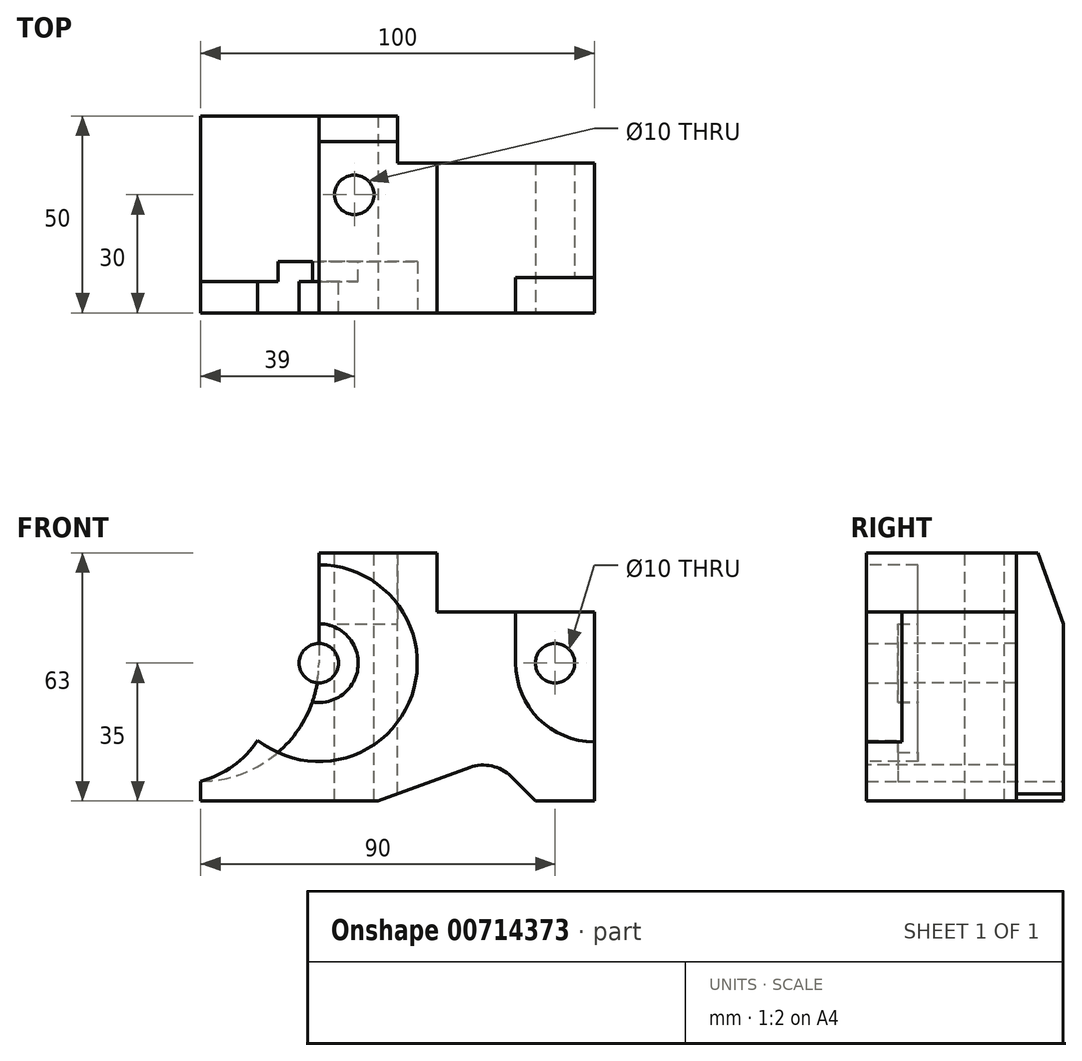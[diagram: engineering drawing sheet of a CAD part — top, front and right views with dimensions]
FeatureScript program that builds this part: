
annotation { "Feature Type Name" : "Feature", "Feature Type Description" : "" }
export const myFeature = defineFeature(function(context is Context, id is Id, definition is map)
    precondition{}
    {
        {
            var Q0;
            Q0=qCreatedBy(makeId("Front.planeOp"),FACE);
            var sketch = newSketch(context, id + "F0", { "sketchPlane" : qUnion([Q0])});
            skLineSegment(sketch, "E0", {"start": v(0, 0) * mm, "end": v(0, 63) * mm});
            skLineSegment(sketch, "E1", {"start": v(0, 63) * mm, "end": v(100, 63) * mm});
            skLineSegment(sketch, "E2", {"start": v(100, 63) * mm, "end": v(100, 0) * mm});
            skLineSegment(sketch, "E3", {"start": v(100, 0) * mm, "end": v(0, 0) * mm});
            skSolve(sketch);
        }
        {
            var Q0;
            Q0 = qSketchRegion(id + "F0", true);
            extrude(context, id + "F1", {"entities" : qUnion([Q0]), "oppositeDirection" : true, "depth" : 50 * mm, "offsetDistance" : 25 * mm});
        }
        {
            var Q0;
            Q0=makeQuery(id+"F1.opExtrude","CAP_FACE",FACE,{"disambiguationData":[OSD([sQuery(id+"F0.wireOp",EDGE,"E0"),sQuery(id+"F0.wireOp",EDGE,"E1"),sQuery(id+"F0.wireOp",EDGE,"E2"),sQuery(id+"F0.wireOp",EDGE,"E3")])],"isStart":true});
            var sketch = newSketch(context, id + "F2", { "sketchPlane" : qUnion([Q0])});
            skLineSegment(sketch, "E4", {"start": v(60, 63) * mm, "end": v(60, 48) * mm});
            skLineSegment(sketch, "E5", {"start": v(60, 48) * mm, "end": v(100, 48) * mm});
            skLineSegment(sketch, "E6", {"start": v(100, 48) * mm, "end": v(100, 63) * mm});
            skLineSegment(sketch, "E7", {"start": v(100, 63) * mm, "end": v(60, 63) * mm});
            skLineSegment(sketch, "E8", {"start": v(80, 48) * mm, "end": v(80, 35) * mm});
            skArc(sketch, "E9", {"start": v(80, 35) * mm, "mid": v(85.86, 20.86) * mm, "end": v(100, 15) * mm});
            skSolve(sketch);
        }
        {
            var Q0;
            Q0 = qSketchRegion(id + "F2", true);
            extrude(context, id + "F3", {"entities" : qUnion([Q0]), "operationType" : NewBodyOperationType.REMOVE, "oppositeDirection" : true, "depth" : 50 * mm, "offsetDistance" : 25 * mm});
        }
        {
            var Q0;
            {var subQ3=sQuery(id+"F2.wireOp",EDGE,"E8");Q0=makeQuery(id+"F2.imprint","IMPRINT",FACE,{"disambiguationData":[TD([[makeQuery(id+"F2.imprint","IMPRINT",EDGE,{"derivedFrom":subQ3}),1.0]])]});}
            extrude(context, id + "F4", {"entities" : qUnion([Q0]), "operationType" : NewBodyOperationType.REMOVE, "oppositeDirection" : true, "depth" : 9 * mm, "offsetDistance" : 25 * mm});
        }
        {
            var Q0;
            Q0=makeQuery(id+"F4.boolean.opBoolean","COPY",FACE,{"derivedFrom":makeQuery(id+"F4.opExtrude","CAP_FACE",FACE,{"disambiguationData":[OSD([sQuery(id+"F0.wireOp",EDGE,"E2"),sQuery(id+"F2.wireOp",EDGE,"E5"),sQuery(id+"F2.wireOp",EDGE,"E8"),sQuery(id+"F2.wireOp",EDGE,"E9")])],"isStart":false})});
            var sketch = newSketch(context, id + "F5", { "sketchPlane" : qUnion([Q0])});
            skCircle(sketch, "E10", {"center": v(90, 35) * mm, "radius": 5 * mm});
            skSolve(sketch);
        }
        {
            var Q0;
            Q0 = qSketchRegion(id + "F5", true);
            extrude(context, id + "F6", {"entities" : qUnion([Q0]), "operationType" : NewBodyOperationType.REMOVE, "oppositeDirection" : true, "depth" : 50 * mm, "offsetDistance" : 25 * mm});
        }
        {
            var Q0;
            Q0=makeQuery(id+"F1.opExtrude","CAP_FACE",FACE,{"disambiguationData":[OSD([sQuery(id+"F0.wireOp",EDGE,"E0"),sQuery(id+"F0.wireOp",EDGE,"E1"),sQuery(id+"F0.wireOp",EDGE,"E2"),sQuery(id+"F0.wireOp",EDGE,"E3")])],"isStart":true});
            var sketch = newSketch(context, id + "F7", { "sketchPlane" : qUnion([Q0])});
            skLineSegment(sketch, "E11", {"start": v(45, 0) * mm, "end": v(85, 0) * mm});
            skLineSegment(sketch, "E12", {"start": v(45, 0) * mm, "end": v(68.34, 8.5) * mm});
            skLineSegment(sketch, "E13", {"start": v(85, 0) * mm, "end": v(78.83, 6.17) * mm});
            skArc(sketch, "E14", {"start": v(78.83, 6.17) * mm, "mid": v(73.92, 8.86) * mm, "end": v(68.34, 8.5) * mm});
            skSolve(sketch);
        }
        {
            var Q0;
            Q0 = qSketchRegion(id + "F7", true);
            extrude(context, id + "F8", {"entities" : qUnion([Q0]), "operationType" : NewBodyOperationType.REMOVE, "oppositeDirection" : true, "depth" : 50 * mm, "offsetDistance" : 25 * mm});
        }
        {
            var Q0;
            Q0=makeQuery(id+"F1.opExtrude","CAP_FACE",FACE,{"disambiguationData":[OSD([sQuery(id+"F0.wireOp",EDGE,"E0"),sQuery(id+"F0.wireOp",EDGE,"E1"),sQuery(id+"F0.wireOp",EDGE,"E2"),sQuery(id+"F0.wireOp",EDGE,"E3")])],"isStart":true});
            var sketch = newSketch(context, id + "F9", { "sketchPlane" : qUnion([Q0])});
            skCircle(sketch, "E15", {"center": v(30, 35) * mm, "radius": 25 * mm});
            skSolve(sketch);
        }
        {
            var Q0;
            Q0 = qSketchRegion(id + "F9", true);
            extrude(context, id + "F10", {"entities" : qUnion([Q0]), "operationType" : NewBodyOperationType.REMOVE, "oppositeDirection" : true, "depth" : 13 * mm, "offsetDistance" : 25 * mm});
        }
        {
            var Q0;
            Q0=makeQuery(id+"F10.boolean.opBoolean","COPY",FACE,{"derivedFrom":makeQuery(id+"F10.opExtrude","CAP_FACE",FACE,{"disambiguationData":[OSD([sQuery(id+"F9.wireOp",EDGE,"E15")])],"isStart":false})});
            var sketch = newSketch(context, id + "F11", { "sketchPlane" : qUnion([Q0])});
            skCircle(sketch, "E16", {"center": v(30, 35) * mm, "radius": 10 * mm});
            skSolve(sketch);
        }
        {
            var Q0;
            Q0 = qSketchRegion(id + "F11", true);
            extrude(context, id + "F12", {"entities" : qUnion([Q0]), "operationType" : NewBodyOperationType.ADD, "depth" : 5 * mm, "offsetDistance" : 25 * mm});
        }
        {
            var Q0;
            Q0=makeQuery(id+"F1.opExtrude","CAP_FACE",FACE,{"disambiguationData":[OSD([sQuery(id+"F0.wireOp",EDGE,"E0"),sQuery(id+"F0.wireOp",EDGE,"E1"),sQuery(id+"F0.wireOp",EDGE,"E2"),sQuery(id+"F0.wireOp",EDGE,"E3")])],"isStart":false});
            var sketch = newSketch(context, id + "F13", { "sketchPlane" : qUnion([Q0])});
            skLineSegment(sketch, "E17", {"start": v(-30, 63) * mm, "end": v(-30, 35) * mm});
            skArc(sketch, "E18", {"start": v(-30, 35) * mm, "mid": v(-21.21, 13.79) * mm, "end": v(0, 5) * mm});
            skLineSegment(sketch, "E19", {"start": v(-30, 63) * mm, "end": v(0, 63) * mm});
            skLineSegment(sketch, "E20", {"start": v(0, 63) * mm, "end": v(0, 5) * mm});
            skSolve(sketch);
        }
        {
            var Q0;
            Q0 = qSketchRegion(id + "F13", true);
            extrude(context, id + "F14", {"entities" : qUnion([Q0]), "operationType" : NewBodyOperationType.REMOVE, "oppositeDirection" : true, "depth" : 42 * mm, "offsetDistance" : 25 * mm});
        }
        {
            var Q0;
            Q0=makeQuery(id+"F14.boolean.opBoolean","COPY",FACE,{"derivedFrom":makeQuery(id+"F14.opExtrude","CAP_FACE",FACE,{"disambiguationData":[OSD([sQuery(id+"F13.wireOp",EDGE,"E17"),sQuery(id+"F13.wireOp",EDGE,"E18"),sQuery(id+"F13.wireOp",EDGE,"E19"),sQuery(id+"F13.wireOp",EDGE,"E20")])],"isStart":false})});
            var sketch = newSketch(context, id + "F15", { "sketchPlane" : qUnion([Q0])});
            skLineSegment(sketch, "E21", {"start": v(-30, 60) * mm, "end": v(-30, 63) * mm});
            skLineSegment(sketch, "E22", {"start": v(-30, 63) * mm, "end": v(0, 63) * mm});
            skLineSegment(sketch, "E23", {"start": v(0, 63) * mm, "end": v(0, 5) * mm});
            skArc(sketch, "E24", {"start": v(-14.47, 15.4) * mm, "mid": v(-8.2, 8.87) * mm, "end": v(0, 5) * mm});
            skArc(sketch, "E25", {"start": v(-14.47, 15.4) * mm, "mid": v(-6.4, 43.22) * mm, "end": v(-30, 60) * mm});
            skSolve(sketch);
        }
        {
            var Q0;
            Q0 = qSketchRegion(id + "F15", true);
            extrude(context, id + "F16", {"entities" : qUnion([Q0]), "operationType" : NewBodyOperationType.REMOVE, "oppositeDirection" : true, "depth" : 8 * mm, "offsetDistance" : 25 * mm});
        }
        {
            var Q0;
            Q0=makeQuery(id+"F12.opExtrude","CAP_FACE",FACE,{"disambiguationData":[OSD([sQuery(id+"F11.wireOp",EDGE,"E16")])],"isStart":false});
            var sketch = newSketch(context, id + "F17", { "sketchPlane" : qUnion([Q0])});
            skCircle(sketch, "E26", {"center": v(30, 35) * mm, "radius": 5 * mm});
            skSolve(sketch);
        }
        {
            var Q0;
            Q0 = qSketchRegion(id + "F17", true);
            extrude(context, id + "F18", {"entities" : qUnion([Q0]), "operationType" : NewBodyOperationType.ADD, "depth" : 8 * mm, "offsetDistance" : 25 * mm});
        }
        {
            var Q0;
            Q0=makeQuery(id+"F1.opExtrude","SWEPT_FACE",FACE,{"disambiguationData":[OSD([sQuery(id+"F0.wireOp",EDGE,"E1")])]});
            var sketch = newSketch(context, id + "F19", { "sketchPlane" : qUnion([Q0])});
            skCircle(sketch, "E27", {"center": v(39, 30) * mm, "radius": 5 * mm});
            skSolve(sketch);
        }
        {
            var Q0;
            Q0 = qSketchRegion(id + "F19", true);
            extrude(context, id + "F20", {"entities" : qUnion([Q0]), "operationType" : NewBodyOperationType.REMOVE, "oppositeDirection" : true, "depth" : 63 * mm, "offsetDistance" : 25 * mm});
        }
        {
            var Q0;
            Q0=makeQuery(id+"F3.boolean.opBoolean","COPY",FACE,{"derivedFrom":makeQuery(id+"F3.opExtrude","SWEPT_FACE",FACE,{"disambiguationData":[OSD([sQuery(id+"F2.wireOp",EDGE,"E4")])]})});
            var sketch = newSketch(context, id + "F21", { "sketchPlane" : qUnion([Q0])});
            skLineSegment(sketch, "E28", {"start": v(50, 63) * mm, "end": v(43.45, 63) * mm});
            skLineSegment(sketch, "E29", {"start": v(43.45, 63) * mm, "end": v(50, 45) * mm});
            skLineSegment(sketch, "E30", {"start": v(50, 45) * mm, "end": v(50, 63) * mm});
            skSolve(sketch);
        }
        {
            var Q0;
            Q0 = qSketchRegion(id + "F21", true);
            extrude(context, id + "F22", {"entities" : qUnion([Q0]), "operationType" : NewBodyOperationType.REMOVE, "oppositeDirection" : true, "depth" : 40 * mm, "offsetDistance" : 25 * mm});
        }
        {
            var Q0;
            Q0=makeQuery(id+"F1.opExtrude","SWEPT_FACE",FACE,{"disambiguationData":[OSD([sQuery(id+"F0.wireOp",EDGE,"E1")])]});
            var sketch = newSketch(context, id + "F23", { "sketchPlane" : qUnion([Q0])});
            skLineSegment(sketch, "E31", {"start": v(50, 38) * mm, "end": v(100, 38) * mm});
            skLineSegment(sketch, "E32", {"start": v(100, 38) * mm, "end": v(100, 50) * mm});
            skLineSegment(sketch, "E33", {"start": v(100, 50) * mm, "end": v(50, 50) * mm});
            skLineSegment(sketch, "E34", {"start": v(50, 50) * mm, "end": v(50, 38) * mm});
            skSolve(sketch);
        }
        {
            var Q0;
            Q0 = qSketchRegion(id + "F23", true);
            extrude(context, id + "F24", {"entities" : qUnion([Q0]), "operationType" : NewBodyOperationType.REMOVE, "oppositeDirection" : true, "depth" : 63 * mm, "offsetDistance" : 25 * mm});
        }
    });
